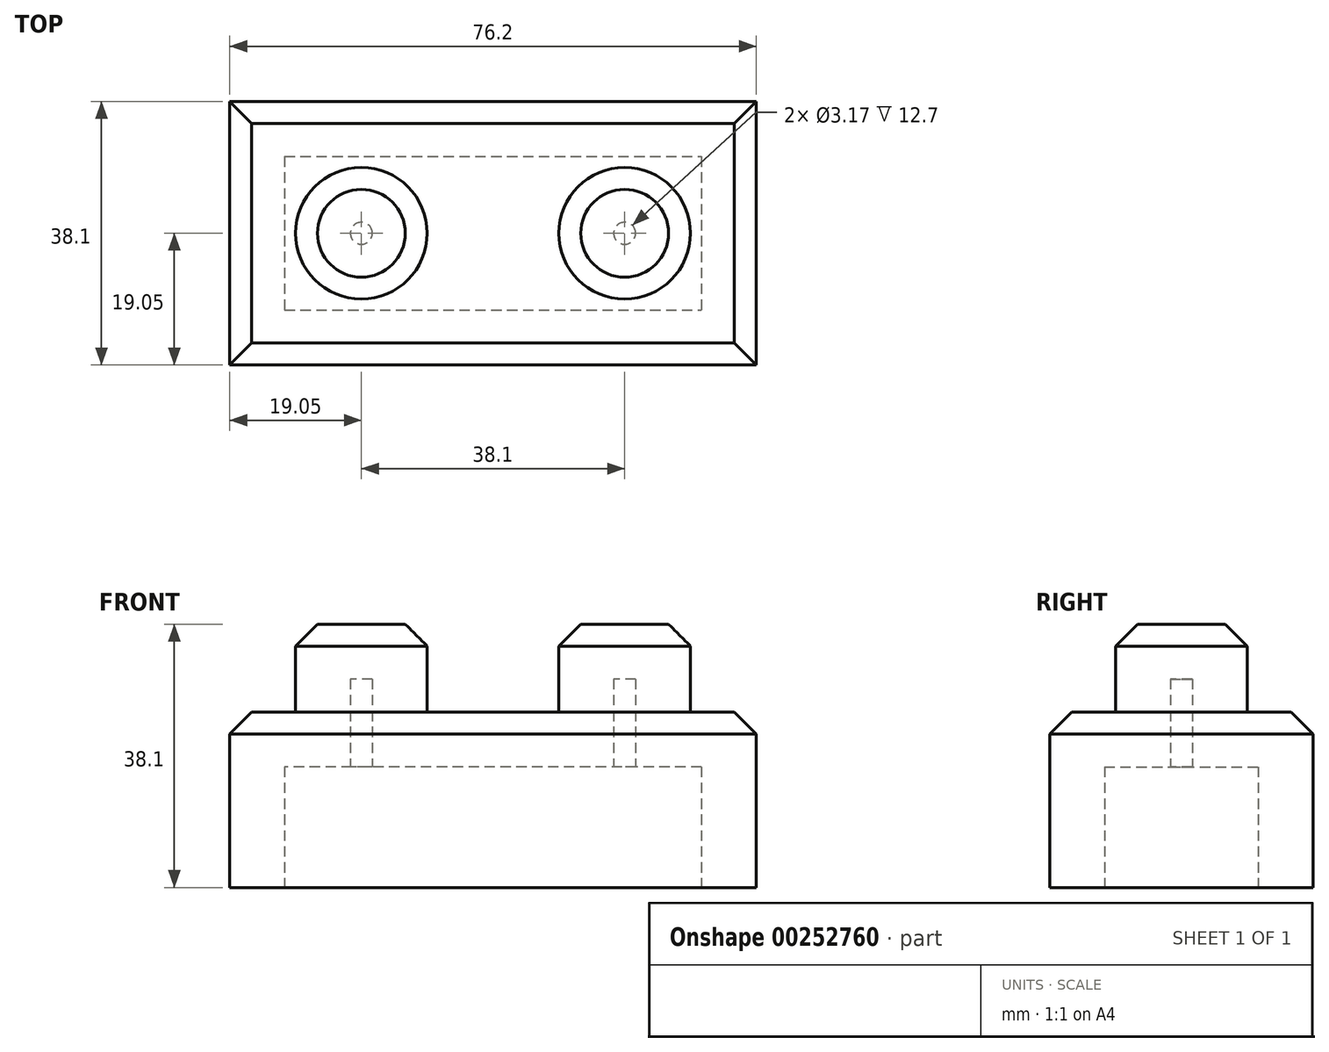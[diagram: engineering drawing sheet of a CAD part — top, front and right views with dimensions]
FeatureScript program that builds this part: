
annotation { "Feature Type Name" : "Feature", "Feature Type Description" : "" }
export const myFeature = defineFeature(function(context is Context, id is Id, definition is map)
    precondition{}
    {
        {
            var Q0;
            Q0=qCreatedBy(makeId("Top.planeOp"),FACE);
            var sketch = newSketch(context, id + "F0", { "sketchPlane" : qUnion([Q0])});
            skLineSegment(sketch, "E0.bottom", {"start": v(0, 0) * mm, "end": v(76.2, 0) * mm});
            skLineSegment(sketch, "E0.top", {"start": v(0, -38.1) * mm, "end": v(76.2, -38.1) * mm});
            skLineSegment(sketch, "E0.left", {"start": v(0, 0) * mm, "end": v(0, -38.1) * mm});
            skLineSegment(sketch, "E0.right", {"start": v(76.2, 0) * mm, "end": v(76.2, -38.1) * mm});
            skSolve(sketch);
        }
        {
            var Q0;
            Q0=makeQuery(id+"F0.imprint","IMPRINT",FACE,{"disambiguationData":[TD([[makeQuery(id+"F0.imprint","IMPRINT",EDGE,{"derivedFrom":sQuery(id+"F0.wireOp",EDGE,"E0.bottom")}),-1.0]])]});
            extrude(context, id + "F1", {"entities" : qUnion([Q0]), "depth" : 25.4 * mm});
        }
        {
            var Q0;
            Q0=makeQuery(id+"F1.opExtrude","CAP_EDGE",EDGE,{"disambiguationData":[OSD([sQuery(id+"F0.wireOp",EDGE,"E0.top")])],"isStart":false});
            var Q1;
            Q1=makeQuery(id+"F1.opExtrude","CAP_EDGE",EDGE,{"disambiguationData":[OSD([sQuery(id+"F0.wireOp",EDGE,"E0.right")])],"isStart":false});
            var Q2;
            Q2=makeQuery(id+"F1.opExtrude","CAP_EDGE",EDGE,{"disambiguationData":[OSD([sQuery(id+"F0.wireOp",EDGE,"E0.bottom")])],"isStart":false});
            var Q3;
            Q3=makeQuery(id+"F1.opExtrude","CAP_EDGE",EDGE,{"disambiguationData":[OSD([sQuery(id+"F0.wireOp",EDGE,"E0.left")])],"isStart":false});
            chamfer(context, id + "F2", {"entities" : qUnion([Q0, Q1, Q2, Q3]), "width" : 3.17 * mm, "tangentPropagation" : true});
        }
        {
            var Q0;
            Q0=makeQuery(id+"F1.opExtrude","CAP_FACE",FACE,{"disambiguationData":[OSD([sQuery(id+"F0.wireOp",EDGE,"E0.bottom"),sQuery(id+"F0.wireOp",EDGE,"E0.top"),sQuery(id+"F0.wireOp",EDGE,"E0.left"),sQuery(id+"F0.wireOp",EDGE,"E0.right")])],"isStart":false});
            var sketch = newSketch(context, id + "F3", { "sketchPlane" : qUnion([Q0])});
            skCircle(sketch, "E1", {"center": v(19.05, -19.05) * mm, "radius": 9.53 * mm});
            skCircle(sketch, "E2", {"center": v(57.15, -19.05) * mm, "radius": 9.53 * mm});
            skSolve(sketch);
        }
        {
            var Q0;
            Q0=makeQuery(id+"F3.imprint","IMPRINT",FACE,{"disambiguationData":[TD([[makeQuery(id+"F3.imprint","IMPRINT",EDGE,{"derivedFrom":sQuery(id+"F3.wireOp",EDGE,"E1")}),1.0]])]});
            var Q1;
            Q1=makeQuery(id+"F3.imprint","IMPRINT",FACE,{"disambiguationData":[TD([[makeQuery(id+"F3.imprint","IMPRINT",EDGE,{"derivedFrom":sQuery(id+"F3.wireOp",EDGE,"E2")}),1.0]])]});
            extrude(context, id + "F4", {"entities" : qUnion([Q0, Q1]), "operationType" : NewBodyOperationType.ADD, "depth" : 12.7 * mm});
        }
        {
            var Q0;
            Q0=makeQuery(id+"F4.opExtrude","CAP_EDGE",EDGE,{"disambiguationData":[OSD([sQuery(id+"F3.wireOp",EDGE,"E1")])],"isStart":false});
            var Q1;
            Q1=makeQuery(id+"F4.opExtrude","CAP_EDGE",EDGE,{"disambiguationData":[OSD([sQuery(id+"F3.wireOp",EDGE,"E2")])],"isStart":false});
            chamfer(context, id + "F5", {"entities" : qUnion([Q0, Q1]), "chamferType" : ChamferType.OFFSET_ANGLE, "width" : 3.17 * mm, "oppositeDirection" : false, "angle" : 45 * degree, "tangentPropagation" : true});
        }
        {
            var Q0;
            Q0=makeQuery(id+"F1.opExtrude","CAP_FACE",FACE,{"disambiguationData":[OSD([sQuery(id+"F0.wireOp",EDGE,"E0.bottom"),sQuery(id+"F0.wireOp",EDGE,"E0.top"),sQuery(id+"F0.wireOp",EDGE,"E0.left"),sQuery(id+"F0.wireOp",EDGE,"E0.right")])],"isStart":true});
            shell(context, id + "F6", {"entities" : qUnion([Q0]), "thickness" : 7.94 * mm});
        }
    });
